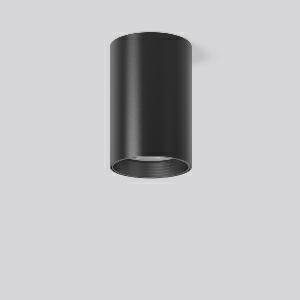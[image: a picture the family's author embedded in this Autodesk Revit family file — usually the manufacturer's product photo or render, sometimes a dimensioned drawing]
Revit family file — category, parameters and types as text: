
# Revit family: heledon_maxi_a_931222_003_2_a2e6
name_source: partatom
category: Lighting Fixtures
units: mm (PartAtom-declared; Revit-internal decimal feet)

## family parameters
Cut with Voids When Loaded = No
Host = Face
Light Source = No
Part Type = Normal
Room Calculation Point = No
Round Connector Dimension = Use Diameter
Shared = No

## types (1)
- HELEDON maxi A (1 x LED Modul 927, 2650 lm, 2700)
    Apparent Load = 25 VA
    Approval mark = CE
    CIE Flux Codes = 96 100 100 100 100
    Color Rendering = 92
    Color Temperature = 2700
    Default Elevation = 1800 mm
    Description = Series: HELEDON maxi
Cylindrical surface-mounted downlight. Housing: die-cast aluminium, powder-coated. Internal ceiling frame polycarbonate with bayonet mounting. Black plastic ring and recessed LED to prevent glare from the side. Optical assembly with lens made of plastic (polycarbonate) for the best homogeneous light distribution - can be changed without tools. Best colour rendering index Ra>90. Suitable for Ceiling mounting. Easy installation with a separate ceiling frame with bayonet mounting and plug connection. Driver integrated. Connected via plug-in connector. High quality converter without flickering and stroboscopic effect. The following accessories can be mounted without use of tools: interchangeable lenses, decorative glasses, honeycomb louvre, clear and frosted diffusers, white interchangeable plastic ring. 
Colour: deep black, matt (RAL 9005)
Diameter: 123 mm
Height: 183 mm
Lamp: LED
Socket: without socket
Colour temperature: 2700K
Colour rendering index (CRI): 92
System power: 25 W
Rated luminous flux: 2650 lm
Luminous efficiency: 106 lm/W
Control gear: Regulated power supply
Protection class: I
Type of protection: IP 20
    Height = 183 mm
    Lamp = 1 x LED Modul 927
    Lamp Light Flux = 2650 lm
    Lamp count = 1
    Length = 123 mm
    Lifetime = 50000 h
    Luminous efficacy = 106 lm/W
    Manufacturer = RZB
    ModVariant = No
    Model = 931222.003.2
    Mounting Place = Ceiling
    Mounting Type = Surface mounted
    Number of Poles = 1
    OnlyDefault = Yes
    Power Factor = 1
    Product Name = HELEDON maxi A
    Product group = Surface mounted downlights
    ProductGroupID = 302
    Protection Class = Protection class I
    Protection Degree = IP 20
    RLX_Detail_Level = 1
    RLX_Emergency_Light_Flux = 0 lm
    RLX_Emergency_Type = 0
    RLX_Emergency_Type_DB = No
    RlxData = <blob elided: 95457 chars, md5=38862b65>
    Socket = socket
    Standby Power = 0 W
    System Light Flux = 2650 lm
    System Power = 25 W
    Type Comments = Product without accessories
    Type Image = 931193.003.jpg
    URL = http://relux.com
    VarID = ---
    Voltage = 230 V
    Voltage Range = 220-240 V
    Weight = 0.00 kg
    Width = 0 mm  [stored 0 ft]

note: [stored X ft] marks values corroborated as IEEE doubles in the binary element streams (Revit-internal decimal feet)

## geometry (parser evidence)
native form markers: Blend x4, Sweep x11
no freeform markers — native parametric forms only
